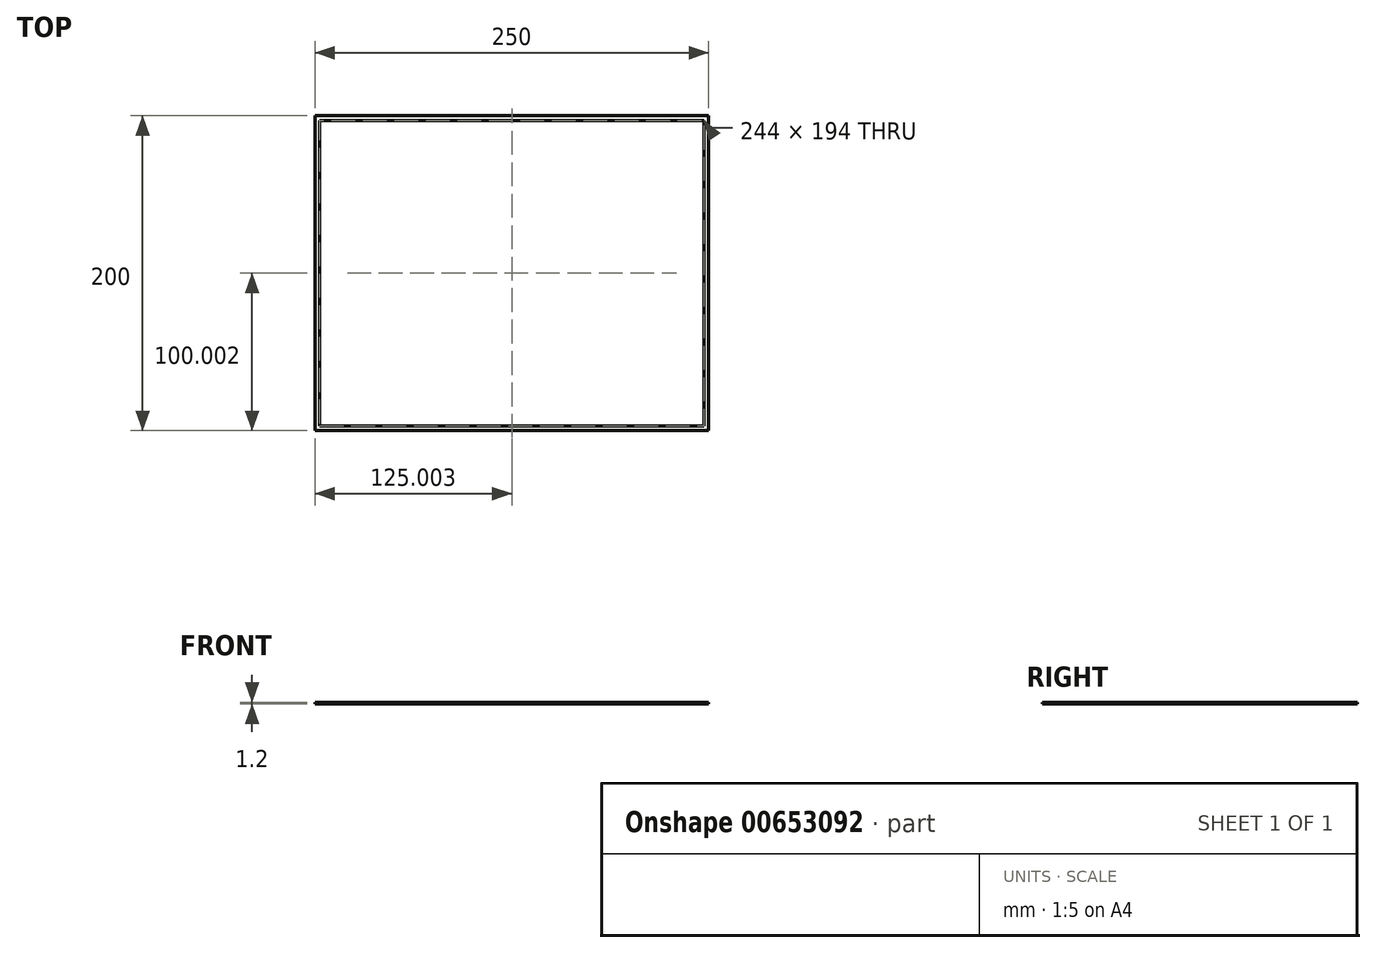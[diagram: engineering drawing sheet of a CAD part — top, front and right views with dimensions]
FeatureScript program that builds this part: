
annotation { "Feature Type Name" : "Feature", "Feature Type Description" : "" }
export const myFeature = defineFeature(function(context is Context, id is Id, definition is map)
    precondition{}
    {
        {
            var Q0;
            Q0=qCreatedBy(makeId("Top.planeOp"),FACE);
            var sketch = newSketch(context, id + "F0", { "sketchPlane" : qUnion([Q0]), "disableImprinting" : false});
            skLineSegment(sketch, "E0.bottom", {"start": v(45.21, 253.1) * mm, "end": v(295.21, 253.1) * mm});
            skLineSegment(sketch, "E0.top", {"start": v(45.21, 53.1) * mm, "end": v(295.21, 53.1) * mm});
            skLineSegment(sketch, "E0.left", {"start": v(45.21, 253.1) * mm, "end": v(45.21, 53.1) * mm});
            skLineSegment(sketch, "E0.right", {"start": v(295.21, 253.1) * mm, "end": v(295.21, 53.1) * mm});
            skLineSegment(sketch, "E1.0", {"start": v(292.21, 250.1) * mm, "end": v(292.21, 56.1) * mm});
            skLineSegment(sketch, "E1.1", {"start": v(48.21, 56.1) * mm, "end": v(292.21, 56.1) * mm});
            skLineSegment(sketch, "E1.2", {"start": v(48.21, 250.1) * mm, "end": v(48.21, 56.1) * mm});
            skLineSegment(sketch, "E1.3", {"start": v(48.21, 250.1) * mm, "end": v(292.21, 250.1) * mm});
            skSolve(sketch);
        }
        {
            var Q0;
            Q0 = qSketchRegion(id + "F0", true);
            var Q1;
            Q1=makeQuery(id+"F0.imprint","IMPRINT",FACE,{"disambiguationData":[TD([[makeQuery(id+"F0.imprint","IMPRINT",EDGE,{"derivedFrom":sQuery(id+"F0.wireOp",EDGE,"E0.bottom")}),-1.0]])]});
            extrude(context, id + "F1", {"entities" : qUnion([Q0, Q1]), "flatOperationType" : FlatOperationType.REMOVE, "depth" : 1.2 * mm, "offsetDistance" : 25 * mm, "domain" : OperationDomain.MODEL});
        }
    });
